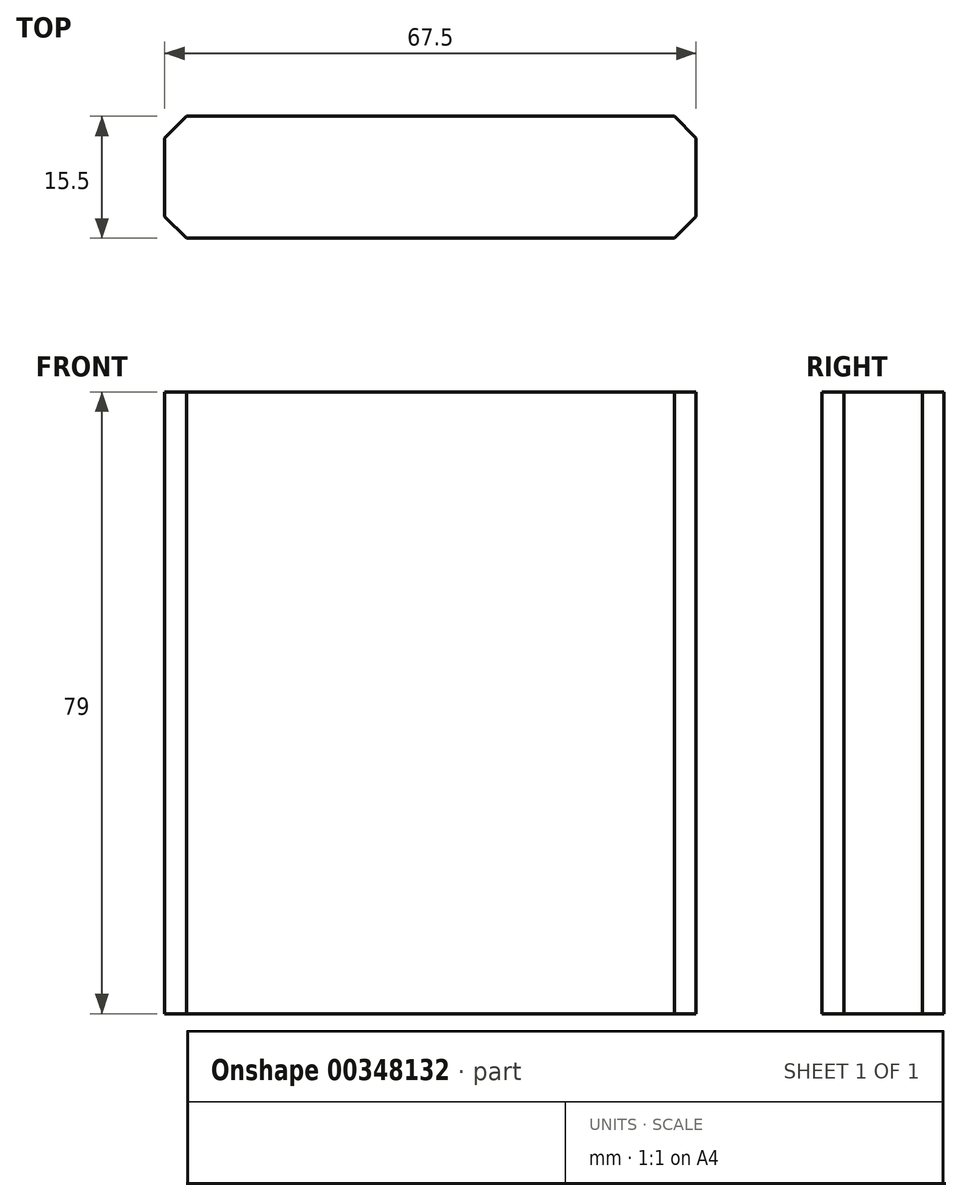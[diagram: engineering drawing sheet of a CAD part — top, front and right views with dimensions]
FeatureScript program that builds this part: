
annotation { "Feature Type Name" : "Feature", "Feature Type Description" : "" }
export const myFeature = defineFeature(function(context is Context, id is Id, definition is map)
    precondition{}
    {
        {
            var Q0;
            Q0=qCreatedBy(makeId("Top.planeOp"),FACE);
            var sketch = newSketch(context, id + "F0", { "sketchPlane" : qUnion([Q0])});
            skLineSegment(sketch, "E0.bottom", {"start": v(33.75, 7.75) * mm, "end": v(-33.75, 7.75) * mm});
            skLineSegment(sketch, "E0.top", {"start": v(33.75, -7.75) * mm, "end": v(-33.75, -7.75) * mm});
            skLineSegment(sketch, "E0.left", {"start": v(33.75, 7.75) * mm, "end": v(33.75, -7.75) * mm});
            skLineSegment(sketch, "E0.right", {"start": v(-33.75, 7.75) * mm, "end": v(-33.75, -7.75) * mm});
            skPoint(sketch, "E0.middle", {"position": v(0, 0) * mm});
            skSolve(sketch);
        }
        {
            var Q0;
            Q0=qCreatedBy(makeId("Front.planeOp"),FACE);
            var sketch = newSketch(context, id + "F1", { "sketchPlane" : qUnion([Q0])});
            skLineSegment(sketch, "E1", {"start": v(0, 0) * mm, "end": v(0, 79) * mm});
            skSolve(sketch);
        }
        {
            var Q0;
            Q0 = qSketchRegion(id + "F0", true);
            var Q1;
            Q1=sQuery(id+"F1.wireOp",EDGE,"E1");
            sweep(context, id + "F2", {"profiles" : qUnion([Q0]), "path" : qUnion([Q1])});
        }
        {
            var Q0;
            Q0=makeQuery(id+"F2.opSweep","SWEPT_EDGE",EDGE,{"disambiguationData":[OSD([sQuery(id+"F0.wireOp",EDGE,"E0.top"),sQuery(id+"F0.wireOp",EDGE,"E0.left"),sQuery(id+"F1.wireOp",EDGE,"E1")])]});
            var Q1;
            Q1=makeQuery(id+"F2.opSweep","SWEPT_EDGE",EDGE,{"disambiguationData":[OSD([sQuery(id+"F0.wireOp",EDGE,"E0.bottom"),sQuery(id+"F0.wireOp",EDGE,"E0.left"),sQuery(id+"F1.wireOp",EDGE,"E1")])]});
            var Q2;
            Q2=makeQuery(id+"F2.opSweep","SWEPT_EDGE",EDGE,{"disambiguationData":[OSD([sQuery(id+"F0.wireOp",EDGE,"E0.top"),sQuery(id+"F0.wireOp",EDGE,"E0.right"),sQuery(id+"F1.wireOp",EDGE,"E1")])]});
            var Q3;
            Q3=makeQuery(id+"F2.opSweep","SWEPT_EDGE",EDGE,{"disambiguationData":[OSD([sQuery(id+"F0.wireOp",EDGE,"E0.bottom"),sQuery(id+"F0.wireOp",EDGE,"E0.right"),sQuery(id+"F1.wireOp",EDGE,"E1")])]});
            chamfer(context, id + "F3", {"entities" : qUnion([Q0, Q1, Q2, Q3]), "width" : 2.75 * mm});
        }
    });
